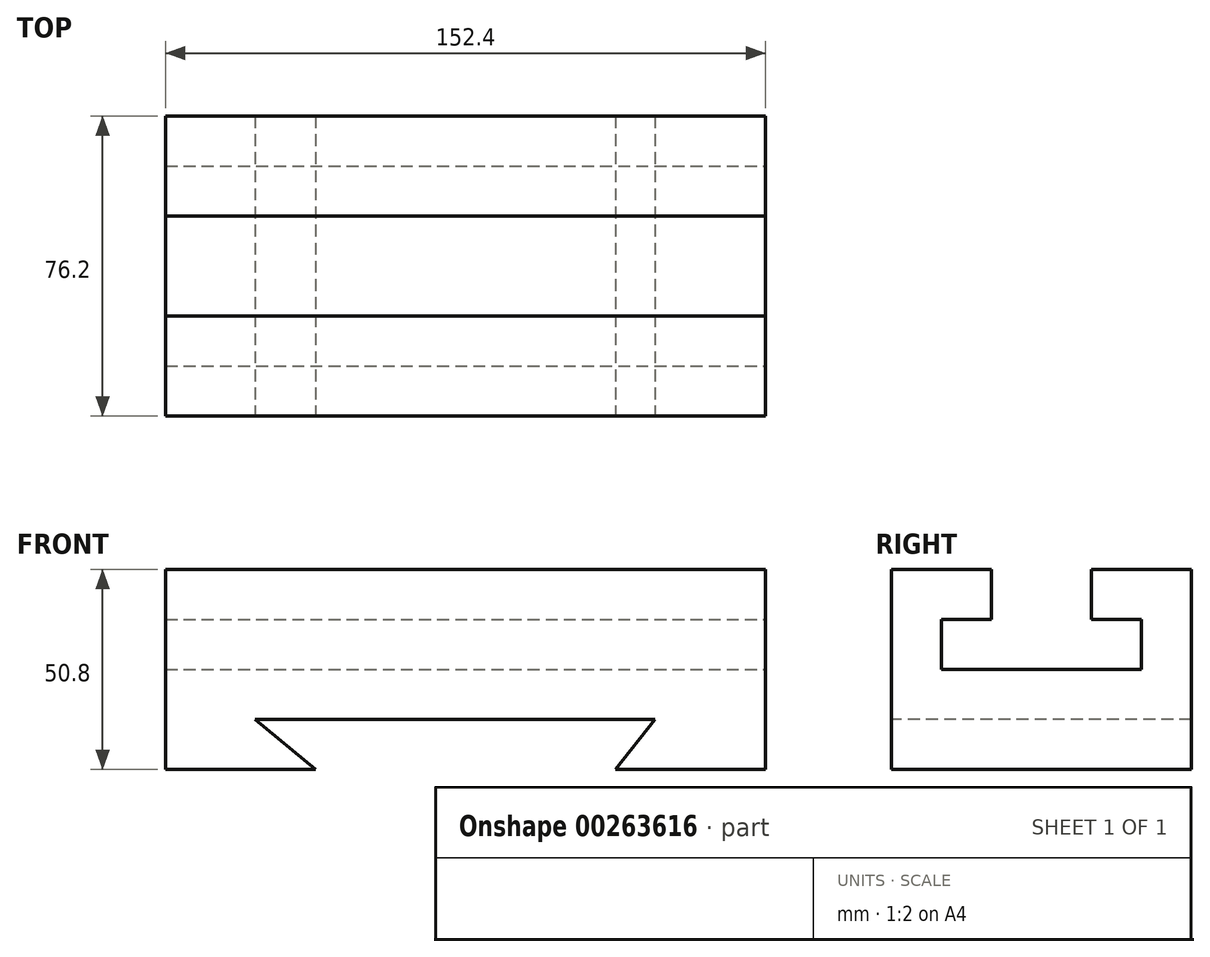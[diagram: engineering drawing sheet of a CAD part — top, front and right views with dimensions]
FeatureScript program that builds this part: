
annotation { "Feature Type Name" : "Feature", "Feature Type Description" : "" }
export const myFeature = defineFeature(function(context is Context, id is Id, definition is map)
    precondition{}
    {
        {
            var Q0;
            Q0=qCreatedBy(makeId("Front.planeOp"),FACE);
            var sketch = newSketch(context, id + "F0", { "sketchPlane" : qUnion([Q0])});
            skLineSegment(sketch, "E0", {"start": v(41.84, -61.56) * mm, "end": v(41.84, -10.76) * mm});
            skLineSegment(sketch, "E1", {"start": v(41.84, -10.76) * mm, "end": v(-110.56, -10.76) * mm});
            skLineSegment(sketch, "E2", {"start": v(41.84, -61.56) * mm, "end": v(3.74, -61.56) * mm});
            skLineSegment(sketch, "E3", {"start": v(3.74, -61.56) * mm, "end": v(13.78, -48.86) * mm});
            skLineSegment(sketch, "E4", {"start": v(13.78, -48.86) * mm, "end": v(-87.82, -48.86) * mm});
            skLineSegment(sketch, "E5", {"start": v(-110.56, -10.76) * mm, "end": v(-110.56, -61.56) * mm});
            skLineSegment(sketch, "E6", {"start": v(-110.56, -61.56) * mm, "end": v(-72.46, -61.56) * mm});
            skLineSegment(sketch, "E7", {"start": v(-72.46, -61.56) * mm, "end": v(-87.82, -48.86) * mm});
            skSolve(sketch);
        }
        {
            var Q0;
            Q0=makeQuery(id+"F0.imprint","IMPRINT",FACE,{"disambiguationData":[TD([[makeQuery(id+"F0.imprint","IMPRINT",EDGE,{"derivedFrom":sQuery(id+"F0.wireOp",EDGE,"E0")}),1.0]])]});
            extrude(context, id + "F1", {"entities" : qUnion([Q0]), "oppositeDirection" : true, "depth" : 76.2 * mm});
        }
        {
            var Q0;
            Q0=makeQuery(id+"F1.opExtrude","SWEPT_FACE",FACE,{"disambiguationData":[OSD([sQuery(id+"F0.wireOp",EDGE,"E0")])]});
            var sketch = newSketch(context, id + "F2", { "sketchPlane" : qUnion([Q0])});
            skLineSegment(sketch, "E8", {"start": v(12.7, -36.16) * mm, "end": v(63.5, -36.16) * mm});
            skLineSegment(sketch, "E9", {"start": v(12.7, -36.16) * mm, "end": v(12.7, -23.46) * mm});
            skLineSegment(sketch, "E10", {"start": v(12.7, -23.46) * mm, "end": v(25.4, -23.46) * mm});
            skLineSegment(sketch, "E11", {"start": v(25.4, -23.46) * mm, "end": v(25.4, -10.76) * mm});
            skLineSegment(sketch, "E12", {"start": v(63.5, -36.16) * mm, "end": v(63.5, -23.46) * mm});
            skLineSegment(sketch, "E13", {"start": v(63.5, -23.46) * mm, "end": v(50.8, -23.46) * mm});
            skLineSegment(sketch, "E14", {"start": v(50.8, -23.46) * mm, "end": v(50.8, -10.76) * mm});
            skLineSegment(sketch, "E15", {"start": v(50.8, -10.76) * mm, "end": v(25.4, -10.76) * mm});
            skSolve(sketch);
        }
        {
            var Q0;
            Q0=makeQuery(id+"F2.imprint","IMPRINT",FACE,{"disambiguationData":[TD([[makeQuery(id+"F2.imprint","IMPRINT",EDGE,{"derivedFrom":sQuery(id+"F2.wireOp",EDGE,"E8")}),1.0]])]});
            extrude(context, id + "F3", {"entities" : qUnion([Q0]), "operationType" : NewBodyOperationType.REMOVE, "oppositeDirection" : true, "depth" : 152.4 * mm});
        }
    });
